# Revit family: WashbasinUnit-80cm-WithDrawer-Vitra-FrameSeries-62286+62287+62288
name_source: partatom
category: Furniture Systems
revit_build: Autodesk Revit 2017 (Build: 20160225_1515(x64)
units: mm (PartAtom-declared; Revit-internal decimal feet)

## family parameters
Cut with Voids When Loaded = No
Host = Face
OmniClass Number = 23.40.00.00
OmniClass Title = Equipment and Furnishings
Part Type = Normal
Room Calculation Point = No
Round Connector Dimension = Use Diameter
Shared = Yes

## types (3) — shared parameters
BIMobject category = Bathroom compound units
Brand = VitrA
Default Elevation = 850 mm  [stored 2.78871 ft]
Design country = Turkey
IFC Classification = Furniture
Main Material = Wood
Manufacturer = VitrA
Manufacturer name = VitrA
Masterformat 2014 Code = 13 42 13
Masterformat 2014 Description = Bathroom Unit Modules
Mounting type = Wall-Hung
NBS Referans Code = 35-75-08
NBS Referans Description = Bathroom Cabinets
Nominal Depth (mm) = 520 mm  [stored 1.70604 ft]
Nominal Height (mm) = 415 mm
Nominal Width (mm) = 800 mm  [stored 2.62467 ft]
OmniClass Code = 23-31 25 13
OmniClass Description = Bathroom Cabinets
Product certification = https://www.vitraglobal.com
Product family = Frame
Product group = Washbasin Unit
Product url = https://www.vitraglobal.com
Technical description = https://www.vitraglobal.com
UNSPSC Code = 301815
UNSPSC Description = Bathroom Cabinets
URL = https://vitraglobal.com
Uniclass 1.4 Code = L8241
Uniclass 1.4 Description = Bathroom Cabinets
Uniclass 2.0 Code = PR-35-75-08
Uniclass 2.0 Description = Bathroom Cabinets
Uniclass 2015 Code = Pr_40_20_93
Uniclass 2015 Name = Wash basins, sinks and troughs
Uniformat II Code = E20
Uniformat II Description = FURNISHINGS
Warranty Period (Year) = 2
Weight Net (kg) = 41
Youtube = https://www.youtube.com

## per-type parameters (varying)
| type | Article No. (default) | Color | Description | Model | Primary Material | Product SKU | Secondary Material |
| WashbasinUnit-80cm-Vitra-FrameSeries-62286 | 62286 | Matt White/Dore Oak | Frame Washbasin Unit - 80cm Matt White/Dore Oak | 62286 | MattWhite | 62286 | Natural Oak |
| WashbasinUnit-80cm-Vitra-FrameSeries-62287 | 62287 | Matt Black/Patterned Black Oak | Frame Washbasin Unit - 80cm Matt Black/Patterned Black Oak | 62287 | Matte Black | 62287 | Black |
| WashbasinUnit-80cm-Vitra-FrameSeries-62288 | 62288 | Matt Taupe/Mocha Oak | Frame Washbasin Unit - 80cm Matt Taupe/Mocha Oak | 62288 | Beige | 62288 | Mocha Oak |

note: [stored X ft] marks values corroborated as IEEE doubles in the binary element streams (Revit-internal decimal feet)

## geometry (parser evidence)
native form markers: Sweep x2
no freeform markers — native parametric forms only
